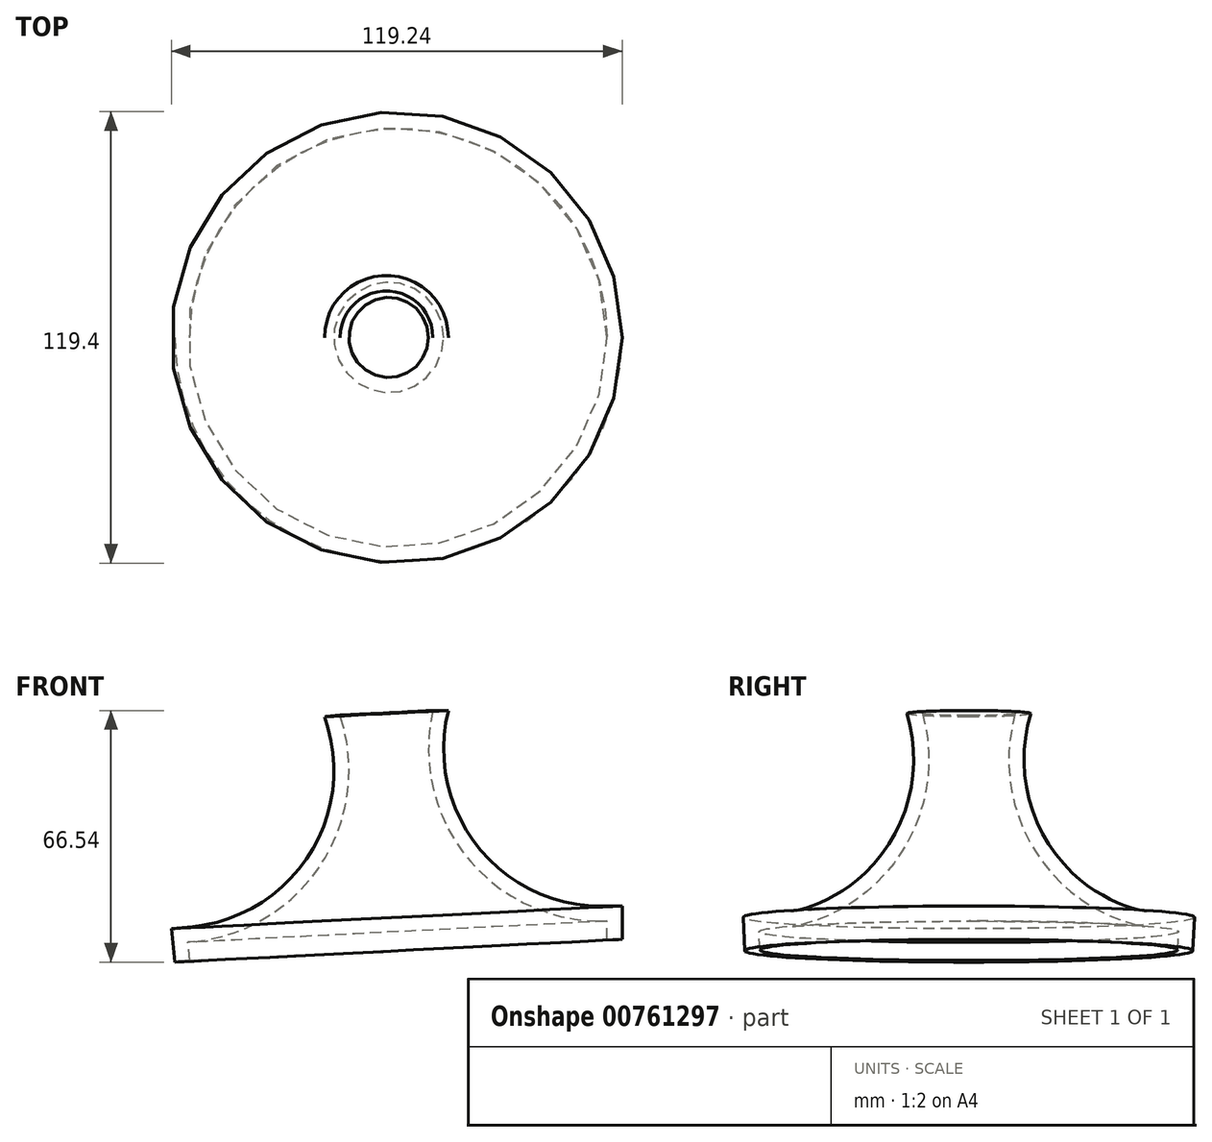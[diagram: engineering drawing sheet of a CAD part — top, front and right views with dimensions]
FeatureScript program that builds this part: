
annotation { "Feature Type Name" : "Feature", "Feature Type Description" : "" }
export const myFeature = defineFeature(function(context is Context, id is Id, definition is map)
    precondition{}
    {
        {
            var Q0;
            Q0=qCreatedBy(makeId("Front.planeOp"),FACE);
            var sketch = newSketch(context, id + "F0", { "sketchPlane" : qUnion([Q0])});
            skLineSegment(sketch, "E0", {"start": v(-13.36, 0) * mm, "end": v(45.97, 0) * mm});
            skLineSegment(sketch, "E1", {"start": v(45.97, 0) * mm, "end": v(45.97, 8.84) * mm});
            skLineSegment(sketch, "E2", {"start": v(45.97, 8.84) * mm, "end": v(40.34, 8.84) * mm});
            skArc(sketch, "E3", {"start": v(0, 60.55) * mm, "mid": v(7.55, 24.85) * mm, "end": v(40.34, 8.84) * mm});
            skLineSegment(sketch, "E4", {"start": v(0, 60.55) * mm, "end": v(-16.42, 60.55) * mm});
            skLineSegment(sketch, "E5", {"start": v(-16.42, 60.55) * mm, "end": v(-13.36, 0) * mm});
            skPoint(sketch, "E6.orphan", {"position": v(0, 0) * mm});
            skSolve(sketch);
        }
        {
            var Q0;
            Q0=makeQuery(id+"F0.imprint","IMPRINT",FACE,{"disambiguationData":[TD([[makeQuery(id+"F0.imprint","IMPRINT",EDGE,{"derivedFrom":sQuery(id+"F0.wireOp",EDGE,"E0")}),1.0]])]});
            var Q1;
            Q1=sQuery(id+"F0.wireOp",EDGE,"E5");
            revolve(context, id + "F1", {"surfaceOperationType" : NewSurfaceOperationType.NEW, "entities" : qUnion([Q0]), "axis" : qUnion([Q1]), "revolveType" : RevolveType.FULL});
        }
        {
            var Q0;
            Q0=makeQuery(id+"F1.opRevolve","SWEPT_FACE",FACE,{"disambiguationData":[OSD([sQuery(id+"F0.wireOp",EDGE,"E4")])]});
            var Q1;
            Q1=makeQuery(id+"F1.opRevolve","SWEPT_FACE",FACE,{"disambiguationData":[OSD([sQuery(id+"F0.wireOp",EDGE,"E0")])]});
            shell(context, id + "F2", {"entities" : qUnion([Q0, Q1]), "thickness" : 4 * mm});
        }
    });
